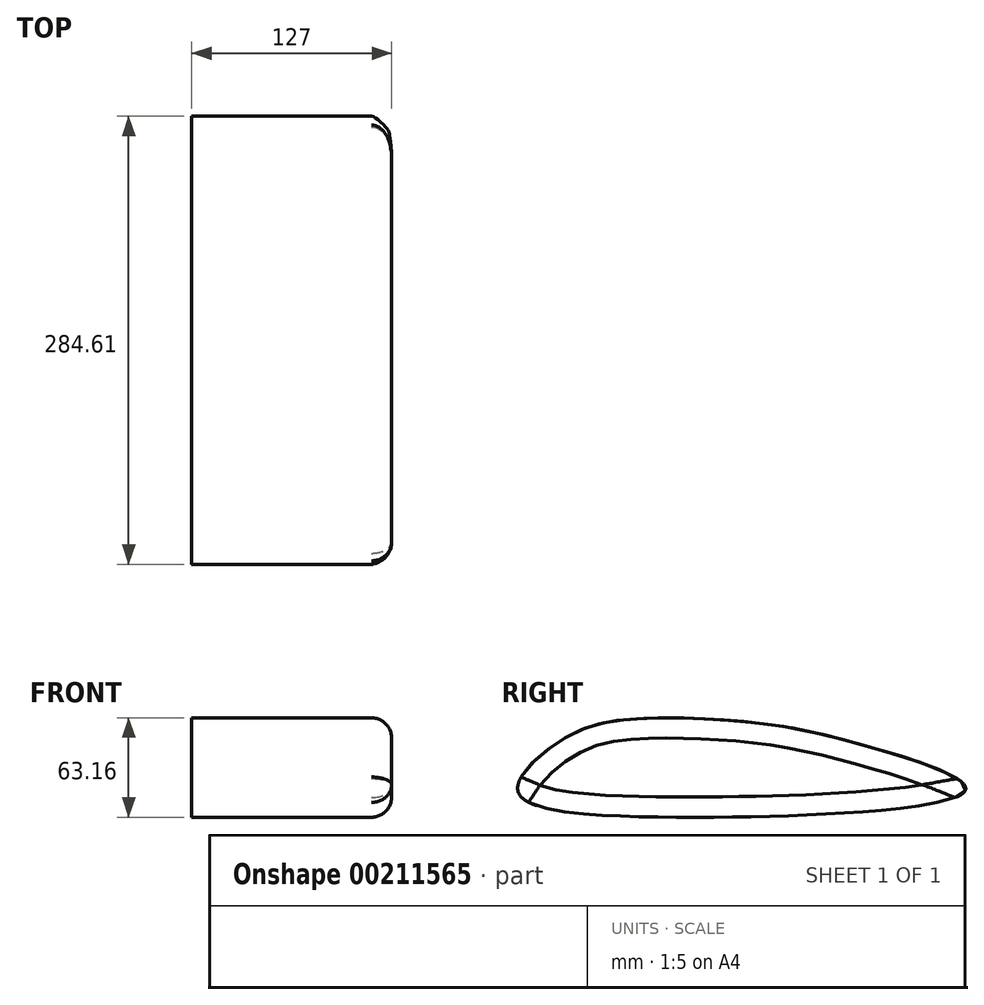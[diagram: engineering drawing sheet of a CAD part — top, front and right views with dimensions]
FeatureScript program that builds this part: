
annotation { "Feature Type Name" : "Feature", "Feature Type Description" : "" }
export const myFeature = defineFeature(function(context is Context, id is Id, definition is map)
    precondition{}
    {
        {
            var Q0;
            Q0=qCreatedBy(makeId("Right.planeOp"),FACE);
            var sketch = newSketch(context, id + "F0", { "sketchPlane" : qUnion([Q0])});
            skFitSpline(sketch, "E0", {"points": [v(0, 0) * mm, v(28.82, 32) * mm, v(74.14, 44.8) * mm, v(146.85, 42.8) * mm, v(216.13, 29.06) * mm, v(284.53, 0) * mm, v(93.44, -17.63) * mm, v(0, 0) * mm]});
            skSolve(sketch);
        }
        {
            var Q0;
            Q0=makeQuery(id+"F0.imprint","IMPRINT",FACE,{"disambiguationData":[TD([[makeQuery(id+"F0.imprint","IMPRINT",EDGE,{"derivedFrom":sQuery(id+"F0.wireOp",EDGE,"E0")}),-1.0]])]});
            extrude(context, id + "F1", {"entities" : qUnion([Q0]), "depth" : 127 * mm});
        }
        {
            var Q0;
            Q0=makeQuery(id+"F1.opExtrude","CAP_EDGE",EDGE,{"disambiguationData":[OSD([sQuery(id+"F0.wireOp",EDGE,"E0")])],"isStart":false});
            fillet(context, id + "F2", {"entities" : qUnion([Q0]), "radius" : 12.88 * mm, "tangentPropagation" : true, "allowEdgeOverflow" : false});
        }
    });
